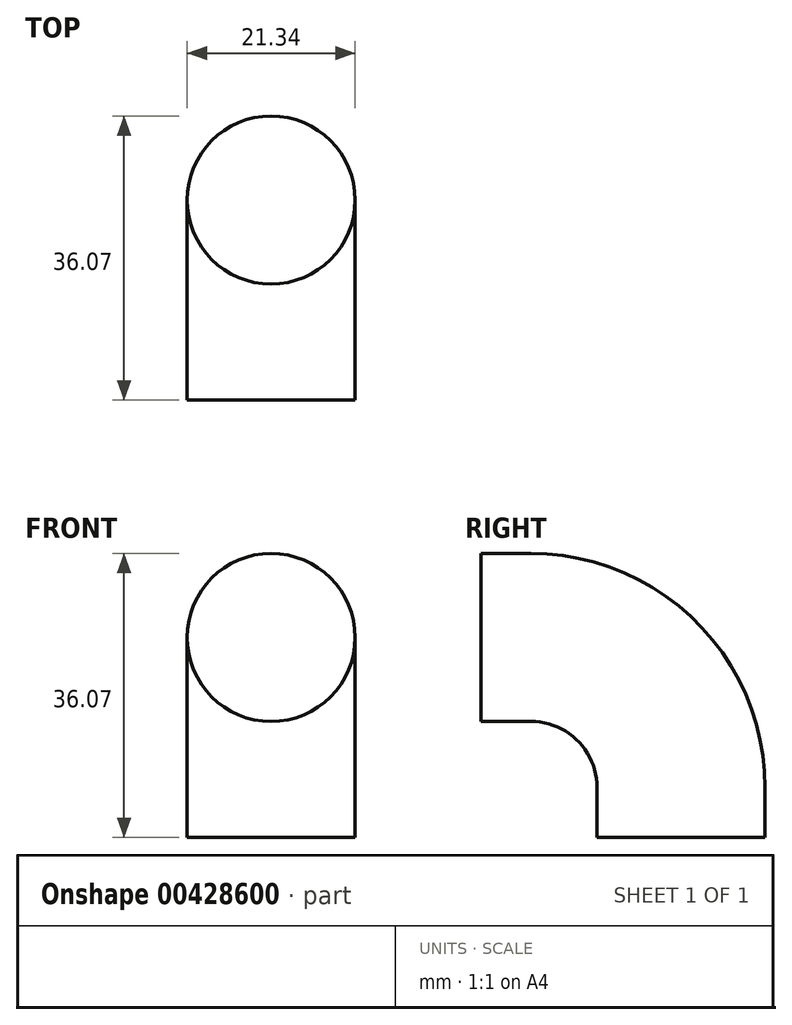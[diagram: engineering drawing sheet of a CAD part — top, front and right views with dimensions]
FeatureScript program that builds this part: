
annotation { "Feature Type Name" : "Feature", "Feature Type Description" : "" }
export const myFeature = defineFeature(function(context is Context, id is Id, definition is map)
    precondition{}
    {
        {
            var Q0;
            Q0=qCreatedBy(makeId("Top.planeOp"),FACE);
            var sketch = newSketch(context, id + "F0", { "sketchPlane" : qUnion([Q0])});
            skCircle(sketch, "E0", {"center": v(0, 46.4) * mm, "radius": 10.67 * mm});
            skSolve(sketch);
        }
        {
            var Q0;
            Q0=qCreatedBy(makeId("Right.planeOp"),FACE);
            var sketch = newSketch(context, id + "F1", { "sketchPlane" : qUnion([Q0])});
            skLineSegment(sketch, "E1", {"start": v(46.4, 0) * mm, "end": v(46.4, 6.35) * mm});
            skLineSegment(sketch, "E2", {"start": v(27.35, 25.4) * mm, "end": v(21, 25.4) * mm});
            skPoint(sketch, "E3.visualSharp", {"position": v(46.4, 25.4) * mm});
            skArc(sketch, "E3.filletArc", {"start": v(46.4, 6.35) * mm, "mid": v(40.82, 19.82) * mm, "end": v(27.35, 25.4) * mm});
            skSolve(sketch);
        }
        {
            var Q0;
            Q0 = qSketchRegion(id + "F1", true);
            var Q1;
            Q1=sQuery(id+"F0.wireOp",EDGE,"E0");
            var Q2;
            Q2=sQuery(id+"F1.wireOp",EDGE,"E1");
            var Q3;
            Q3=sQuery(id+"F1.wireOp",EDGE,"E3.filletArc");
            var Q4;
            Q4=sQuery(id+"F1.wireOp",EDGE,"E2");
            sweep(context, id + "F2", {"bodyType" : ToolBodyType.SURFACE, "profiles" : qUnion([Q0]), "surfaceProfiles" : qUnion([Q1]), "path" : qUnion([Q2, Q3, Q4])});
        }
    });
